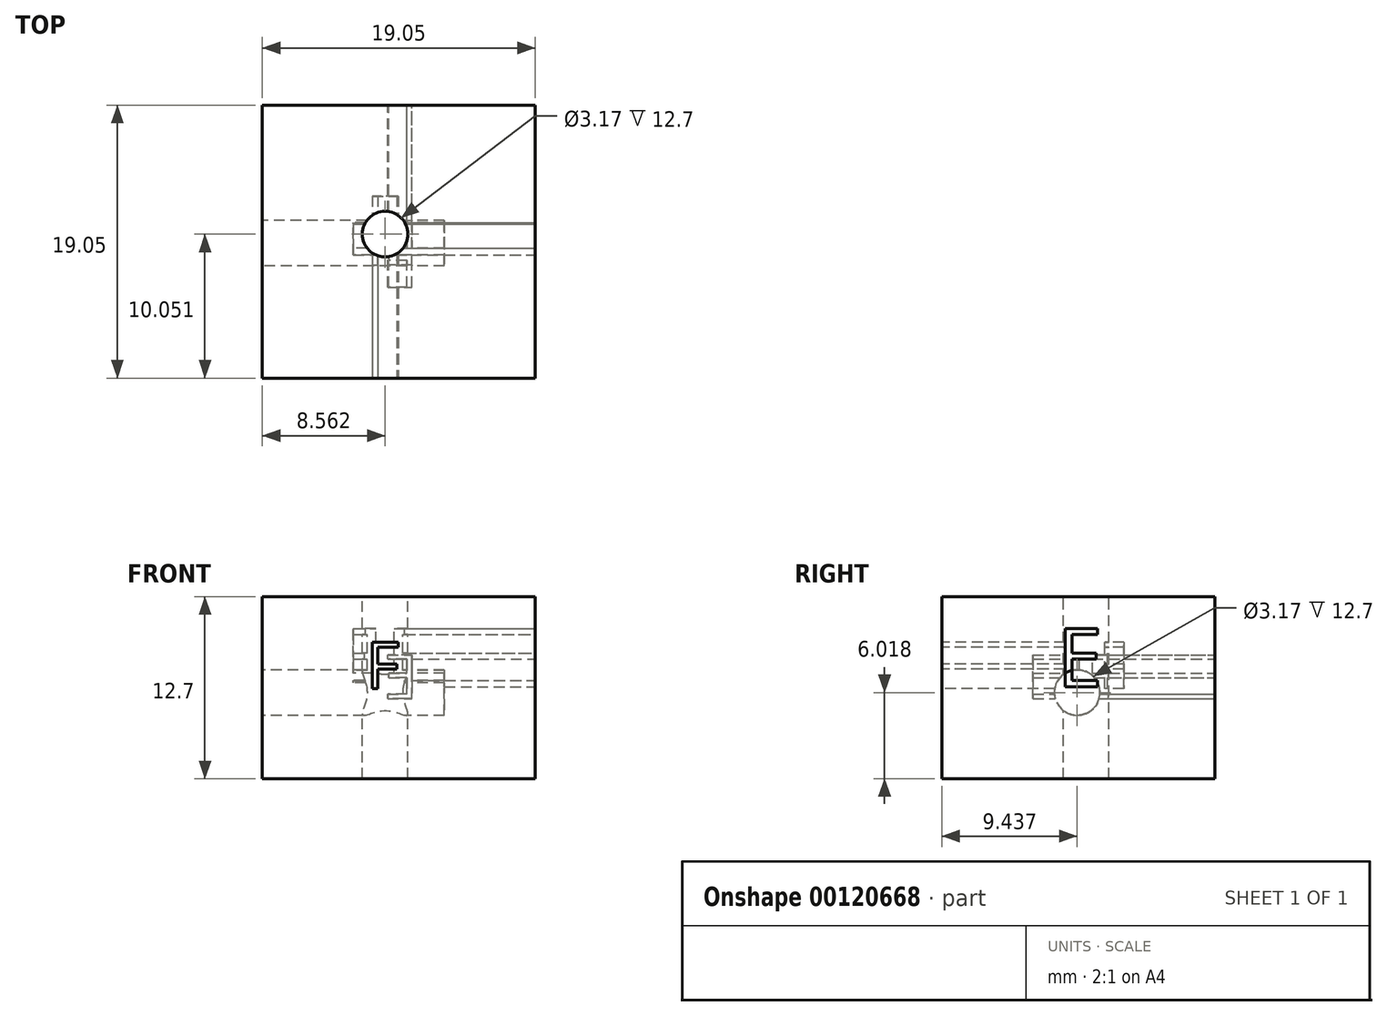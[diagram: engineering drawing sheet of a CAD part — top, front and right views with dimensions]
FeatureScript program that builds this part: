
annotation { "Feature Type Name" : "Feature", "Feature Type Description" : "" }
export const myFeature = defineFeature(function(context is Context, id is Id, definition is map)
    precondition{}
    {
        {
            var Q0;
            Q0=qCreatedBy(makeId("Top.planeOp"),FACE);
            var sketch = newSketch(context, id + "F0", { "sketchPlane" : qUnion([Q0])});
            skLineSegment(sketch, "E0.bottom", {"start": v(-10.3, 10.12) * mm, "end": v(8.76, 10.12) * mm});
            skLineSegment(sketch, "E0.top", {"start": v(-10.3, -8.93) * mm, "end": v(8.76, -8.93) * mm});
            skLineSegment(sketch, "E0.left", {"start": v(-10.3, 10.12) * mm, "end": v(-10.3, -8.93) * mm});
            skLineSegment(sketch, "E0.right", {"start": v(8.76, 10.12) * mm, "end": v(8.76, -8.93) * mm});
            skSolve(sketch);
        }
        {
            var Q0;
            Q0=makeQuery(id+"F0.imprint","IMPRINT",FACE,{"disambiguationData":[TD([[makeQuery(id+"F0.imprint","IMPRINT",EDGE,{"derivedFrom":sQuery(id+"F0.wireOp",EDGE,"E0.bottom")}),-1.0]])]});
            extrude(context, id + "F1", {"entities" : qUnion([Q0]), "depth" : 12.7 * mm});
        }
        {
            var Q0;
            Q0=makeQuery(id+"F1.opExtrude","CAP_FACE",FACE,{"disambiguationData":[OSD([sQuery(id+"F0.wireOp",EDGE,"E0.bottom"),sQuery(id+"F0.wireOp",EDGE,"E0.top"),sQuery(id+"F0.wireOp",EDGE,"E0.left"),sQuery(id+"F0.wireOp",EDGE,"E0.right")])],"isStart":false});
            var sketch = newSketch(context, id + "F2", { "sketchPlane" : qUnion([Q0])});
            skCircle(sketch, "E1", {"center": v(-1.73, 1.12) * mm, "radius": 1.59 * mm});
            skSolve(sketch);
        }
        {
            var Q0;
            Q0=makeQuery(id+"F2.imprint","IMPRINT",FACE,{"disambiguationData":[TD([[makeQuery(id+"F2.imprint","IMPRINT",EDGE,{"derivedFrom":sQuery(id+"F2.wireOp",EDGE,"E1")}),1.0]])]});
            extrude(context, id + "F3", {"entities" : qUnion([Q0]), "operationType" : NewBodyOperationType.REMOVE, "oppositeDirection" : true, "depth" : 19.05 * mm});
        }
        {
            var Q0;
            Q0=makeQuery(id+"F1.opExtrude","SWEPT_FACE",FACE,{"disambiguationData":[OSD([sQuery(id+"F0.wireOp",EDGE,"E0.top")])]});
            var sketch = newSketch(context, id + "F4", { "sketchPlane" : qUnion([Q0])});
            skText(sketch, "E2", { "text": "F", "fontName": "OpenSans-Regular.ttf"});
            const initialGuessF4  = {"E2": [-0.00306, 0.00629, 1, 0, 0.00325]};
            skSetInitialGuess(sketch, initialGuessF4);
            skSolve(sketch);
        }
        {
            var Q0;
            Q0=makeQuery(id+"F4.imprint","IMPRINT",FACE,{"disambiguationData":[TD([[makeQuery(id+"F4.imprint","IMPRINT",EDGE,{"derivedFrom":sQuery(id+"F4.wireOp",EDGE,"E2.sketch_text.stroke-0")}),-1.0]])]});
            extrude(context, id + "F5", {"entities" : qUnion([Q0]), "operationType" : NewBodyOperationType.REMOVE, "oppositeDirection" : true, "depth" : 12.7 * mm});
        }
        {
            var Q0;
            Q0=makeQuery(id+"F1.opExtrude","SWEPT_FACE",FACE,{"disambiguationData":[OSD([sQuery(id+"F0.wireOp",EDGE,"E0.right")])]});
            var sketch = newSketch(context, id + "F6", { "sketchPlane" : qUnion([Q0])});
            skText(sketch, "E3", { "text": "E", "fontName": "OpenSans-Regular.ttf"});
            const initialGuessF6  = {"E3": [-0.00089, 0.00643, 1, 0, 0.0041]};
            skSetInitialGuess(sketch, initialGuessF6);
            skSolve(sketch);
        }
        {
            var Q0;
            Q0=makeQuery(id+"F6.imprint","IMPRINT",FACE,{"disambiguationData":[TD([[makeQuery(id+"F6.imprint","IMPRINT",EDGE,{"derivedFrom":sQuery(id+"F6.wireOp",EDGE,"E3.sketch_text.stroke-0")}),-1.0]])]});
            extrude(context, id + "F7", {"entities" : qUnion([Q0]), "operationType" : NewBodyOperationType.REMOVE, "oppositeDirection" : true, "depth" : 12.7 * mm});
        }
        {
            var Q0;
            Q0=makeQuery(id+"F1.opExtrude","SWEPT_FACE",FACE,{"disambiguationData":[OSD([sQuery(id+"F0.wireOp",EDGE,"E0.bottom")])]});
            var sketch = newSketch(context, id + "F8", { "sketchPlane" : qUnion([Q0])});
            skText(sketch, "E4", { "text": "E", "fontName": "OpenSans-Regular.ttf"});
            const initialGuessF8  = {"E4": [-0.00057, 0.0056, 1, 0, 0.00308]};
            skSetInitialGuess(sketch, initialGuessF8);
            skSolve(sketch);
        }
        {
            var Q0;
            Q0=makeQuery(id+"F8.imprint","IMPRINT",FACE,{"disambiguationData":[TD([[makeQuery(id+"F8.imprint","IMPRINT",EDGE,{"derivedFrom":sQuery(id+"F8.wireOp",EDGE,"E4.sketch_text.stroke-0")}),-1.0]])]});
            extrude(context, id + "F9", {"entities" : qUnion([Q0]), "operationType" : NewBodyOperationType.REMOVE, "oppositeDirection" : true, "depth" : 12.7 * mm});
        }
        {
            var Q0;
            Q0=makeQuery(id+"F1.opExtrude","SWEPT_FACE",FACE,{"disambiguationData":[OSD([sQuery(id+"F0.wireOp",EDGE,"E0.left")])]});
            var sketch = newSketch(context, id + "F10", { "sketchPlane" : qUnion([Q0])});
            skCircle(sketch, "E5", {"center": v(-0.5, 6.02) * mm, "radius": 1.59 * mm});
            skSolve(sketch);
        }
        {
            var Q0;
            Q0=makeQuery(id+"F10.imprint","IMPRINT",FACE,{"disambiguationData":[TD([[makeQuery(id+"F10.imprint","IMPRINT",EDGE,{"derivedFrom":sQuery(id+"F10.wireOp",EDGE,"E5")}),1.0]])]});
            extrude(context, id + "F11", {"entities" : qUnion([Q0]), "operationType" : NewBodyOperationType.REMOVE, "oppositeDirection" : true, "depth" : 12.7 * mm});
        }
    });
